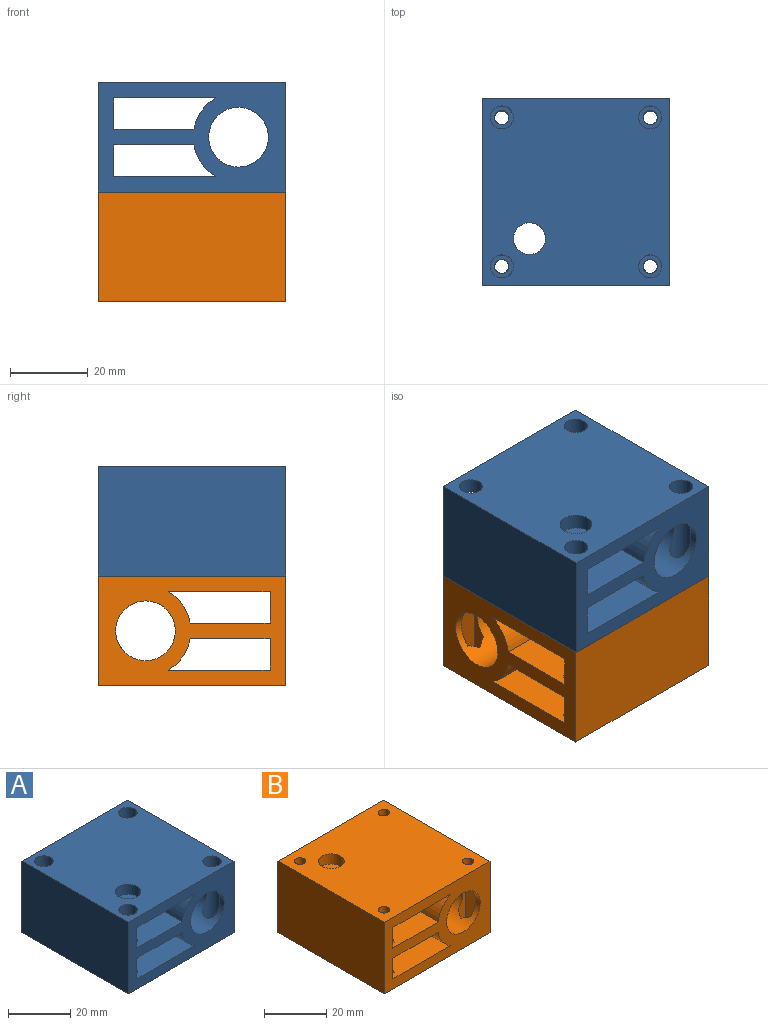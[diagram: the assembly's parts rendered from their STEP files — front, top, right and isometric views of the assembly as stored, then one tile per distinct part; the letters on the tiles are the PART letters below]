
ASSEMBLY  parts=2 mates=1
PART A: 34 faces, bbox 48.3x48.4x28.3 mm
  f0: plane 32.8x8.13mm, normal (1,0,0), area 266.5mm2, adj f7,f9,f23,f25
  f1: plane 8.13x2.2mm, normal (1,0,0), area 17.9mm2, adj f7,f9,f18,f23
  f2: plane 32.8x8.13mm, normal (1,0,0), area 266.5mm2, adj f11,f15,f23,f25
  f3: plane 8.13x2.2mm, normal (1,0,0), area 17.9mm2, adj f11,f15,f18,f23
  f4: plane 48.4x48.25mm, normal (0,0,-1), area 2240mm2, adj f5,f13,f17,f18,f27,f28,f29,f30
  f5: plane 48.4x28.25mm, normal (1,0,0), area 1367.3mm2, adj f4,f6,f17,f18
  f6: plane 48.4x48.25mm, normal (0,0,1), area 2170.6mm2, adj f5,f13,f17,f18,f19,f21,f23,f25
  f7: plane 48.4x20.6mm, normal (0,0,1), area 904mm2, adj f0,f1,f8,f14,f17,f18,f23,f25
  f8: plane 8.13x2.2mm, normal (1,0,0), area 17.9mm2, adj f7,f9,f17,f25
  f9: plane 48.4x26.26mm, normal (0,0,-1), area 1178.1mm2, adj f0,f1,f8,f14,f17,f18,f23,f25
  f10: plane 8.13x2.2mm, normal (1,0,0), area 17.9mm2, adj f11,f15,f17,f25
  f11: plane 48.4x20.6mm, normal (0,0,-1), area 904mm2, adj f2,f3,f10,f12,f17,f18,f23,f25
  f12: cylinder r=11.7mm len=48.4mm, axis (0,1,0), area 495mm2, adj f11,f15,f17,f18
  f13: plane 48.4x28.25mm, normal (-1,0,0), area 1367.3mm2, adj f4,f6,f17,f18
  f14: cylinder r=11.7mm len=48.4mm, axis (0,1,0), area 495mm2, adj f7,f9,f17,f18
  f15: plane 48.4x26.26mm, normal (0,0,1), area 1178.1mm2, adj f2,f3,f10,f12,f17,f18,f23,f25
  f16: cylinder r=7.7mm len=48.4mm, axis (0,1,0), area 2178.4mm2, adj f17,f18,f19,f21
  f17: plane 48.25x28.25mm, normal (0,-1,0), area 810.7mm2, adj f4,f5,f6,f7,f8,f9,f10,f11
  f18: plane 48.25x28.25mm, normal (0,1,0), area 810.7mm2, adj f1,f3,f4,f5,f6,f7,f9,f11
  f19: cylinder r=2.98mm len=25.25mm, axis (0,0,1), area 364.9mm2, adj f6,f16,f20
  f20: plane 5.95x5.95mm, normal (0,0,1), area 17.3mm2, adj f19,f30
  f21: cylinder r=2.98mm len=25.25mm, axis (0,0,1), area 364.9mm2, adj f6,f16,f22
  f22: plane 5.95x5.95mm, normal (0,0,1), area 17.3mm2, adj f21,f29
  f23: cylinder r=2.98mm len=25.25mm, axis (0,0,1), area 287mm2, adj f0,f1,f2,f3,f6,f7,f9,f11
  f24: plane 5.95x5.95mm, normal (0,0,1), area 17.3mm2, adj f23,f28
  f25: cylinder r=2.98mm len=25.25mm, axis (0,0,1), area 287mm2, adj f0,f2,f6,f7,f8,f9,f10,f11
  f26: plane 5.95x5.95mm, normal (0,0,1), area 17.3mm2, adj f25,f27
  f27: cylinder r=1.82mm len=3.65mm, axis (0,0,-1), area 34.4mm2, adj f4,f26
  f28: cylinder r=1.82mm len=3.65mm, axis (0,0,-1), area 34.4mm2, adj f4,f24
  f29: cylinder r=1.82mm len=3.65mm, axis (0,0,-1), area 34.4mm2, adj f4,f22
  f30: cylinder r=1.82mm len=3.65mm, axis (0,0,-1), area 34.4mm2, adj f4,f20
  f31: cylinder r=4.12mm len=8.25mm, axis (0,0,-1), area 103.7mm2, adj f4,f15
  f32: cylinder r=4.12mm len=8.25mm, axis (0,0,-1), area 103.7mm2, adj f7,f11
  f33: cylinder r=4.12mm len=8.25mm, axis (0,0,-1), area 103.7mm2, adj f6,f9
PART B: 74 faces, bbox 48.3x48.4x28.3 mm
  f0: plane 32.65x8.13mm, normal (1,0,0), area 265.3mm2, adj f4,f6,f33,f47
  f1: plane 8.13x2.13mm, normal (1,0,0), area 17.3mm2, adj f4,f6,f21,f42
  f2: plane 32.65x8.13mm, normal (1,0,0), area 265.3mm2, adj f8,f9,f33,f47
  f3: plane 8.13x2.13mm, normal (1,0,0), area 17.3mm2, adj f8,f9,f21,f42
  f4: plane 48.4x20.6mm, normal (0,0,1), area 903.3mm2, adj f0,f1,f5,f20,f21,f22,f28,f30
  f5: plane 8.13x2.13mm, normal (1,0,0), area 17.3mm2, adj f4,f6,f22,f32
  f6: plane 48.4x26.26mm, normal (0,0,-1), area 1177.5mm2, adj f0,f1,f5,f20,f21,f22,f29,f32
  f7: plane 8.13x2.13mm, normal (1,0,0), area 17.3mm2, adj f8,f9,f22,f32
  f8: plane 48.4x20.6mm, normal (0,0,-1), area 903.3mm2, adj f2,f3,f7,f18,f21,f22,f28,f30
  f9: plane 48.4x26.26mm, normal (0,0,1), area 1177.5mm2, adj f2,f3,f7,f18,f21,f22,f27,f31
  f10: cylinder r=7.7mm len=48.4mm, axis (0,1,0), area 2178.2mm2, adj f21,f22,f54,f55,f58,f61,f62,f63
  f11: cylinder r=1.82mm len=3.65mm, axis (0,0,-1), area 34.4mm2, adj f15,f66
  f12: cylinder r=1.82mm len=3.65mm, axis (0,0,-1), area 34.4mm2, adj f15,f56
  f13: cylinder r=1.82mm len=3.65mm, axis (0,0,-1), area 34.4mm2, adj f15,f48
  f14: cylinder r=1.82mm len=3.65mm, axis (0,0,-1), area 34.4mm2, adj f15,f36
  f15: plane 48.4x48.25mm, normal (0,0,-1), area 2240mm2, adj f11,f12,f13,f14,f16,f19,f21,f22
  f16: plane 48.4x28.25mm, normal (1,0,0), area 1367.3mm2, adj f15,f17,f21,f22
  f17: plane 48.4x48.25mm, normal (0,0,1), area 2240mm2, adj f16,f19,f21,f22,f23,f24,f25,f26
  f18: cylinder r=11.7mm len=48.4mm, axis (0,1,0), area 495mm2, adj f8,f9,f21,f22
  f19: plane 48.4x28.25mm, normal (-1,0,0), area 1367.3mm2, adj f15,f17,f21,f22
  f20: cylinder r=11.7mm len=48.4mm, axis (0,1,0), area 495mm2, adj f4,f6,f21,f22
  f21: plane 48.25x28.25mm, normal (0,-1,0), area 810.7mm2, adj f1,f3,f4,f6,f8,f9,f10,f15
  f22: plane 48.25x28.25mm, normal (0,1,0), area 810.7mm2, adj f4,f5,f6,f7,f8,f9,f10,f15
  f23: cylinder r=1.82mm len=3.65mm, axis (0,0,-1), area 34.4mm2, adj f17,f67
  f24: cylinder r=1.82mm len=3.65mm, axis (0,0,-1), area 34.4mm2, adj f17,f57
  f25: cylinder r=1.82mm len=3.65mm, axis (0,0,-1), area 34.4mm2, adj f17,f49
  f26: cylinder r=1.82mm len=3.65mm, axis (0,0,-1), area 34.4mm2, adj f17,f37
  f27: cylinder r=4.12mm len=8.25mm, axis (0,0,-1), area 103.7mm2, adj f9,f15
  f28: cylinder r=4.12mm len=8.25mm, axis (0,0,-1), area 103.7mm2, adj f4,f8
  f29: cylinder r=4.12mm len=8.25mm, axis (0,0,-1), area 103.7mm2, adj f6,f17
  f30: plane 4x2.88mm, normal (-0.87,-0.5,0), area 13.3mm2, adj f4,f8,f32,f34
  f31: plane 2.88x1.66mm, normal (-0.87,-0.5,0), area 3.3mm2, adj f9,f32,f35,f36
  f32: plane 22.25x3.32mm, normal (0,-1,0), area 30.6mm2, adj f4,f5,f6,f7,f8,f9,f30,f31
  f33: plane 22.25x3.32mm, normal (0,1,0), area 30.6mm2, adj f0,f2,f4,f6,f8,f9,f34,f35
  f34: plane 4x2.88mm, normal (-0.87,0.5,0), area 13.3mm2, adj f4,f8,f30,f33
  f35: plane 2.88x1.66mm, normal (-0.87,0.5,0), area 3.3mm2, adj f9,f31,f33,f36
  f36: plane 6.64x5.75mm, normal (0,0,1), area 18.2mm2, adj f14,f31,f32,f33,f35,f39,f40
  f37: plane 6.64x5.75mm, normal (0,0,-1), area 18.2mm2, adj f26,f32,f33,f38,f39,f40,f41
  f38: plane 2.88x1.66mm, normal (-0.87,-0.5,0), area 3.3mm2, adj f6,f32,f37,f41
  f39: plane 22.25x2.88mm, normal (0.87,-0.5,0), area 73.9mm2, adj f32,f36,f37,f40
  f40: plane 22.25x2.88mm, normal (0.87,0.5,0), area 73.9mm2, adj f33,f36,f37,f39
  f41: plane 2.88x1.66mm, normal (-0.87,0.5,0), area 3.3mm2, adj f6,f33,f37,f38
  f42: plane 22.25x3.32mm, normal (0,1,0), area 30.6mm2, adj f1,f3,f4,f6,f8,f9,f43,f44
  f43: plane 4x2.88mm, normal (-0.87,0.5,0), area 13.3mm2, adj f4,f8,f42,f45
  f44: plane 2.88x1.66mm, normal (-0.87,0.5,0), area 3.3mm2, adj f9,f42,f46,f48
  f45: plane 4x2.88mm, normal (-0.87,-0.5,0), area 13.3mm2, adj f4,f8,f43,f47
  f46: plane 2.88x1.66mm, normal (-0.87,-0.5,0), area 3.3mm2, adj f9,f44,f47,f48
  f47: plane 22.25x3.32mm, normal (0,-1,0), area 30.6mm2, adj f0,f2,f4,f6,f8,f9,f45,f46
  f48: plane 6.64x5.75mm, normal (0,0,1), area 18.2mm2, adj f13,f42,f44,f46,f47,f52,f53
  f49: plane 6.64x5.75mm, normal (0,0,-1), area 18.2mm2, adj f25,f42,f47,f50,f51,f52,f53
  f50: plane 2.88x1.66mm, normal (-0.87,0.5,0), area 3.3mm2, adj f6,f42,f49,f51
  f51: plane 2.88x1.66mm, normal (-0.87,-0.5,0), area 3.3mm2, adj f6,f47,f49,f50
  f52: plane 22.25x2.88mm, normal (0.87,-0.5,0), area 73.9mm2, adj f47,f48,f49,f53
  f53: plane 22.25x2.88mm, normal (0.87,0.5,0), area 73.9mm2, adj f42,f48,f49,f52
  f54: plane 5.7x2.88mm, normal (0.87,-0.5,0), area 16.6mm2, adj f10,f55,f57,f61
  f55: plane 5.7x2.88mm, normal (0.87,0.5,0), area 16.6mm2, adj f10,f54,f57,f58
  f56: plane 6.64x5.75mm, normal (0,0,1), area 18.2mm2, adj f12,f58,f59,f60,f61,f62,f63
  f57: plane 6.64x5.75mm, normal (0,0,-1), area 18.2mm2, adj f24,f54,f55,f58,f59,f60,f61
  f58: plane 22.25x3.32mm, normal (0,1,0), area 57.2mm2, adj f10,f55,f56,f57,f59,f63
  f59: plane 22.25x2.88mm, normal (-0.87,0.5,0), area 73.9mm2, adj f56,f57,f58,f60
  f60: plane 22.25x2.88mm, normal (-0.87,-0.5,0), area 73.9mm2, adj f56,f57,f59,f61
  f61: plane 22.25x3.32mm, normal (0,-1,0), area 57.2mm2, adj f10,f54,f56,f57,f60,f62
  f62: plane 5.7x2.88mm, normal (0.87,-0.5,0), area 16.6mm2, adj f10,f56,f61,f63
  f63: plane 5.7x2.88mm, normal (0.87,0.5,0), area 16.6mm2, adj f10,f56,f58,f62
  f64: plane 5.7x2.88mm, normal (0.87,-0.5,0), area 16.6mm2, adj f10,f65,f67,f68
  f65: plane 5.7x2.88mm, normal (0.87,0.5,0), area 16.6mm2, adj f10,f64,f67,f71
  f66: plane 6.64x5.75mm, normal (0,0,1), area 18.2mm2, adj f11,f68,f69,f70,f71,f72,f73
  f67: plane 6.64x5.75mm, normal (0,0,-1), area 18.2mm2, adj f23,f64,f65,f68,f71,f72,f73
  f68: plane 22.25x3.32mm, normal (0,-1,0), area 57.2mm2, adj f10,f64,f66,f67,f69,f73
  f69: plane 5.7x2.88mm, normal (0.87,-0.5,0), area 16.6mm2, adj f10,f66,f68,f70
  f70: plane 5.7x2.88mm, normal (0.87,0.5,0), area 16.6mm2, adj f10,f66,f69,f71
  f71: plane 22.25x3.32mm, normal (0,1,0), area 57.2mm2, adj f10,f65,f66,f67,f70,f72
  f72: plane 22.25x2.88mm, normal (-0.87,0.5,0), area 73.9mm2, adj f66,f67,f71,f73
  f73: plane 22.25x2.88mm, normal (-0.87,-0.5,0), area 73.9mm2, adj f66,f67,f68,f72
PLACE A t=(-5.5,-0.8,3.56)mm
PLACE B rot(axis=(0,0,1),90deg) t=(-5.5,-0.8,-24.69)mm
MATE fastened B.f27 <-> A.f31  axis (0,0,1) through (-17.5,-12.8,-10.56)mm
